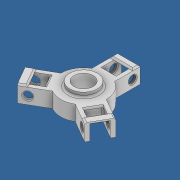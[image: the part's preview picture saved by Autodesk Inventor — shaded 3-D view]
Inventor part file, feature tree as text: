
AUTODESK INVENTOR PART (.ipt)
format: ipt  version: 2022 (Build 260153000, 153)  size: 363,520 bytes
history: native  units: in
note: dims shown in document units (in); Inventor stores cm internally (conversion verified against a paired STEP export)
features: sketch x10, extrude x9, chamfer x6, fillet x4, pattern_circular x1, shell x1, thread x1
ambient origin geometry x8: Origin, YZ Plane, XZ Plane, XY Plane, X Axis, Y Axis, Z Axis, Center Point
bodies: Solid1 (feature_tree)
feature tree (32):
  extrude  "Extrusion1"  Depth=3.9016in
  extrude  "Extrusion2"  Depth=0.3937in
  extrude  "Extrusion3"  Depth=0.3937in
  fillet  "Fillet4"  Radius=3.8583in
  extrude  "Extrusion8"  Depth=0.3937in TaperAngle=0.0deg
  chamfer  "Chamfer2"  Distance=0.7874in
  chamfer  "Chamfer3"  Distance=0.0394in
  pattern_circular  "Circular Pattern4"  Angle=45.0deg  [1 undecoded]
  sketch  "Sketch11"  dims[d16=0.0in]
  chamfer  "Chamfer4"  Distance=1.1811in Angle=360.0deg
  chamfer  "Chamfer5"  Distance=0.0394in Angle=45.0deg
  shell  "Shell1"  Thickness=0.0394in
  extrude  "Extrusion9"  Depth=0.0625in
  extrude  "Extrusion10"  Depth=0.0787in
  chamfer  "Chamfer6"  Distance=0.3937in
  chamfer  "Chamfer7"  Distance=0.5in
  fillet  "Fillet6"  Radius=0.3937in
  thread  "Thread2"  [1 undecoded]
  extrude  "Extrusion11"  Depth=0.0394in TaperAngle=45.0deg
  fillet  "Fillet7"  Radius=0.0354in
  extrude  "Extrusion13"  Depth=0.0787in TaperAngle=0.0deg
  extrude  "Extrusion14"  Depth=0.1181in TaperAngle=0.0deg
  fillet  "Fillet8"  Radius=0.0492in
  sketch  "Sketch1"  dims[d0=1.1811in d1=3.9016in]
  sketch  "Sketch2"  dims[d2=0.3937in d3=0.0in d4=0.2953in]
  sketch  "Sketch4"  dims[d5=0.689in d8=0.3937in d9=3.8583in]
  sketch  "Sketch10"  dims[d10=0.4921in d11=0.3937in d12=0.0in]
  sketch  "Sketch12"  dims[d17=0.1969in d18=0.7874in d19=0.0in]
  sketch  "Sketch13"  dims[d34=0.0197in]
  sketch  "Sketch14"  dims[d45=0.59in]
  sketch  "Sketch16"  dims[d46=0.1969in d47=0.0394in d48=0.0in]
  sketch  "Sketch17"  dims[d49=0.0394in d50=0.0492in d51=45.0deg d52=0.0394in d53=0.0492in d54=45.0deg d55=1.1811in d56=360.0deg d58=0.0394in d59=0.0492in d60=45.0deg d61=0.0394in d62=0.0492in d63=45.0deg d64=0.0625in d65=0.5in d66=0.3937in d67=0.0in d68=0.5in d69=0.3937in d70=0.0in d73=0.0394in d74=0.0492in d75=45.0deg d76=0.0394in d77=0.0492in d78=45.0deg d79=0.0354in d80=0.5512in d81=0.0in d82=0.1181in d83=0.0in d89=0.0492in d91=0.5in d92=0.5906in d93=0.0591in d94=0.0in d95=0.5in d96=0.0591in d97=0.0in d98=0.0787in]
note: 2 required parameter values undecoded (feature->parameter linkage not recoverable at this tier; creation-order binding heuristic only, values carry confidence <= 0.55)
